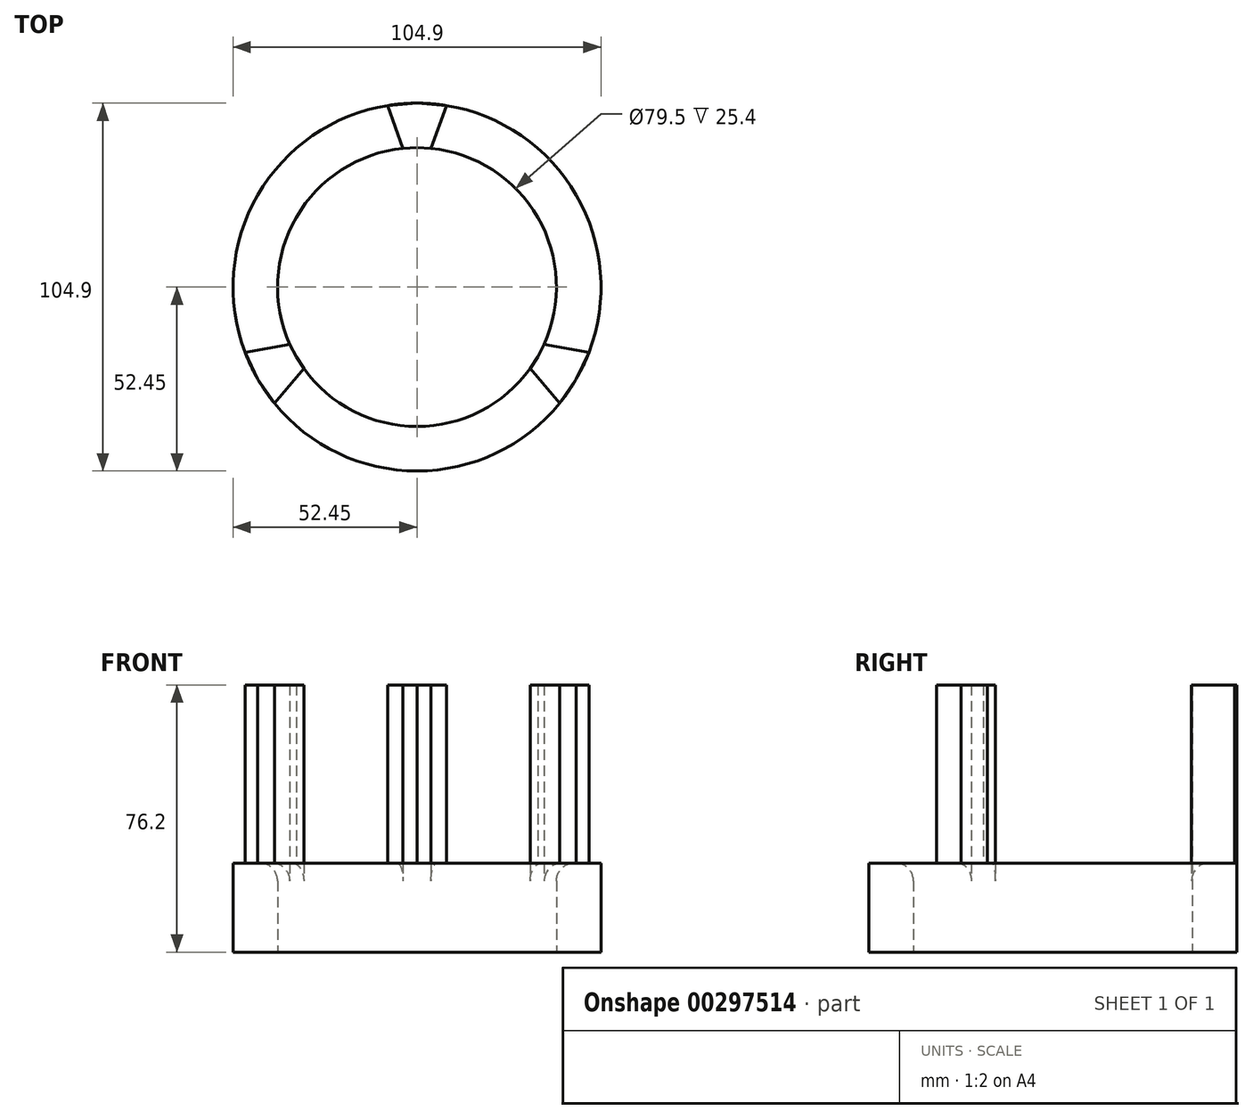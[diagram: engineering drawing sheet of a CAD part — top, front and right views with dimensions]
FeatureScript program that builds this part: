
annotation { "Feature Type Name" : "Feature", "Feature Type Description" : "" }
export const myFeature = defineFeature(function(context is Context, id is Id, definition is map)
    precondition{}
    {
        {
            var Q0;
            Q0=qCreatedBy(makeId("Top.planeOp"),FACE);
            var sketch = newSketch(context, id + "F0", { "sketchPlane" : qUnion([Q0])});
            skCircle(sketch, "E0", {"center": v(0, 0) * mm, "radius": 39.75 * mm});
            skCircle(sketch, "E1.0", {"center": v(0, 0) * mm, "radius": 52.45 * mm});
            skSolve(sketch);
        }
        {
            var Q0;
            Q0 = qSketchRegion(id + "F0", true);
            extrude(context, id + "F1", {"entities" : qUnion([Q0]), "depth" : 25.4 * mm});
        }
        {
            var Q0;
            Q0=makeQuery(id+"F1.opExtrude","CAP_FACE",FACE,{"disambiguationData":[OSD([sQuery(id+"F0.wireOp",EDGE,"E0"),sQuery(id+"F0.wireOp",EDGE,"E1.0")])],"isStart":false});
            var sketch = newSketch(context, id + "F2", { "sketchPlane" : qUnion([Q0])});
            skLineSegment(sketch, "E2", {"start": v(3.98, 39.55) * mm, "end": v(8.37, 51.78) * mm});
            skLineSegment(sketch, "E3", {"start": v(0, 52.45) * mm, "end": v(8.37, 51.78) * mm});
            skLineSegment(sketch, "E4", {"start": v(0, 39.75) * mm, "end": v(3.98, 39.55) * mm});
            skLineSegment(sketch, "E5.MirrorCS", {"start": v(0, 52.45) * mm, "end": v(-8.37, 51.78) * mm});
            skLineSegment(sketch, "E6.MirrorCS", {"start": v(-3.98, 39.55) * mm, "end": v(-8.37, 51.78) * mm});
            skLineSegment(sketch, "E7", {"start": v(0, 39.75) * mm, "end": v(-3.98, 39.55) * mm});
            skLineSegment(sketch, "E8.1.0", {"start": v(-45.42, -26.23) * mm, "end": v(-40.66, -33.14) * mm});
            skLineSegment(sketch, "E8.1.1", {"start": v(-32.26, -23.22) * mm, "end": v(-40.66, -33.14) * mm});
            skLineSegment(sketch, "E8.1.2", {"start": v(-34.43, -19.88) * mm, "end": v(-32.26, -23.22) * mm});
            skLineSegment(sketch, "E8.1.3", {"start": v(-34.43, -19.88) * mm, "end": v(-36.24, -16.33) * mm});
            skLineSegment(sketch, "E8.1.4", {"start": v(-36.24, -16.33) * mm, "end": v(-49.03, -18.64) * mm});
            skLineSegment(sketch, "E8.1.5", {"start": v(-45.42, -26.23) * mm, "end": v(-49.03, -18.64) * mm});
            skLineSegment(sketch, "E8.2.0", {"start": v(45.42, -26.23) * mm, "end": v(49.03, -18.64) * mm});
            skLineSegment(sketch, "E8.2.1", {"start": v(36.24, -16.33) * mm, "end": v(49.03, -18.64) * mm});
            skLineSegment(sketch, "E8.2.2", {"start": v(34.43, -19.88) * mm, "end": v(36.24, -16.33) * mm});
            skLineSegment(sketch, "E8.2.3", {"start": v(34.43, -19.88) * mm, "end": v(32.26, -23.22) * mm});
            skLineSegment(sketch, "E8.2.4", {"start": v(32.26, -23.22) * mm, "end": v(40.66, -33.14) * mm});
            skLineSegment(sketch, "E8.2.5", {"start": v(45.42, -26.23) * mm, "end": v(40.66, -33.14) * mm});
            skPoint(sketch, "E8.center", {"position": v(0, 0) * mm});
            skSolve(sketch);
        }
        {
            var Q0;
            Q0 = qSketchRegion(id + "F2", true);
            extrude(context, id + "F3", {"entities" : qUnion([Q0]), "operationType" : NewBodyOperationType.ADD, "depth" : 50.8 * mm});
        }
        {
            var Q0;
            {var subQ0=sQuery(id+"F2.wireOp",EDGE,"E6.MirrorCS");var subQ2=sQuery(id+"F0.wireOp",EDGE,"E0");var subQ3=makeQuery(id+"F1.opExtrude","CAP_FACE",FACE,{"disambiguationData":[OSD([subQ2,sQuery(id+"F0.wireOp",EDGE,"E1.0")])],"isStart":false});var subQ4=makeQuery(id+"F1.opExtrude","SWEPT_FACE",FACE,{"disambiguationData":[OSD([subQ2])]});Q0=makeQuery(id+"F3.boolean.opBoolean","SPLIT",EDGE,{"disambiguationData":[topologyDisambiguationEdgeConnected([subQ4,subQ3]),TD([makeQuery(id+"F3.opExtrude","SWEPT_FACE",FACE,{"disambiguationData":[OSD([subQ0])]})])],"derivedFrom":makeQuery(id+"F1.opExtrude","CAP_EDGE",EDGE,{"disambiguationData":[OSD([subQ2])],"isStart":false})});}
            var Q1;
            {var subQ1=sQuery(id+"F2.wireOp",EDGE,"E2");var subQ2=sQuery(id+"F0.wireOp",EDGE,"E0");var subQ3=makeQuery(id+"F1.opExtrude","CAP_FACE",FACE,{"disambiguationData":[OSD([subQ2,sQuery(id+"F0.wireOp",EDGE,"E1.0")])],"isStart":false});var subQ4=makeQuery(id+"F1.opExtrude","SWEPT_FACE",FACE,{"disambiguationData":[OSD([subQ2])]});Q1=makeQuery(id+"F3.boolean.opBoolean","SPLIT",EDGE,{"disambiguationData":[topologyDisambiguationEdgeConnected([subQ4,subQ3]),TD([makeQuery(id+"F3.opExtrude","SWEPT_FACE",FACE,{"disambiguationData":[OSD([subQ1])]})])],"derivedFrom":makeQuery(id+"F1.opExtrude","CAP_EDGE",EDGE,{"disambiguationData":[OSD([subQ2])],"isStart":false})});}
            var Q2;
            {var subQ0=sQuery(id+"F2.wireOp",EDGE,"E8.1.1");var subQ3=sQuery(id+"F0.wireOp",EDGE,"E0");var subQ4=makeQuery(id+"F1.opExtrude","CAP_FACE",FACE,{"disambiguationData":[OSD([subQ3,sQuery(id+"F0.wireOp",EDGE,"E1.0")])],"isStart":false});var subQ5=makeQuery(id+"F1.opExtrude","SWEPT_FACE",FACE,{"disambiguationData":[OSD([subQ3])]});Q2=makeQuery(id+"F3.boolean.opBoolean","SPLIT",EDGE,{"disambiguationData":[topologyDisambiguationEdgeConnected([subQ5,subQ4]),TD([makeQuery(id+"F3.opExtrude","SWEPT_FACE",FACE,{"disambiguationData":[OSD([subQ0])]})])],"derivedFrom":makeQuery(id+"F1.opExtrude","CAP_EDGE",EDGE,{"disambiguationData":[OSD([subQ3])],"isStart":false})});}
            fillet(context, id + "F4", {"entities" : qUnion([Q0, Q1, Q2]), "radius" : 5.08 * mm, "tangentPropagation" : true, "allowEdgeOverflow" : false});
        }
    });
